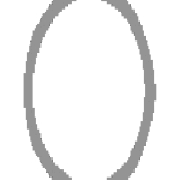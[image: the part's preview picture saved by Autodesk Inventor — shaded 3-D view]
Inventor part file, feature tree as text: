
AUTODESK INVENTOR PART (.ipt)
format: ipt  version: 2021 (Build 250183000, 183)  size: 111,616 bytes
history: native  units: in
note: dims shown in document units (in); Inventor stores cm internally (conversion verified against a paired STEP export)
features: other x4, sketch x3, plane x1
ambient origin geometry x8: Origin, YZ Plane, XZ Plane, XY Plane, X Axis, Y Axis, Z Axis, Center Point
bodies: Solid1 (feature_tree), Body (feature_tree)
feature tree (8):
  other  "Driven Length"
  other  "Frame Generator"
  other  "Start Plane"
  other  "End Plane"
  sketch  "Sketch"  dims[d2=20.2683in d4=-0.0in d5=20.2683in d6=0.12in d7=0.0in d8=90.0deg d9=20.2683in]
  sketch  "Sketch2"  dims[d0=1.0in]
  plane  "Work Plane3"
  sketch  "Sketch3"  dims[d1=0.065in]
